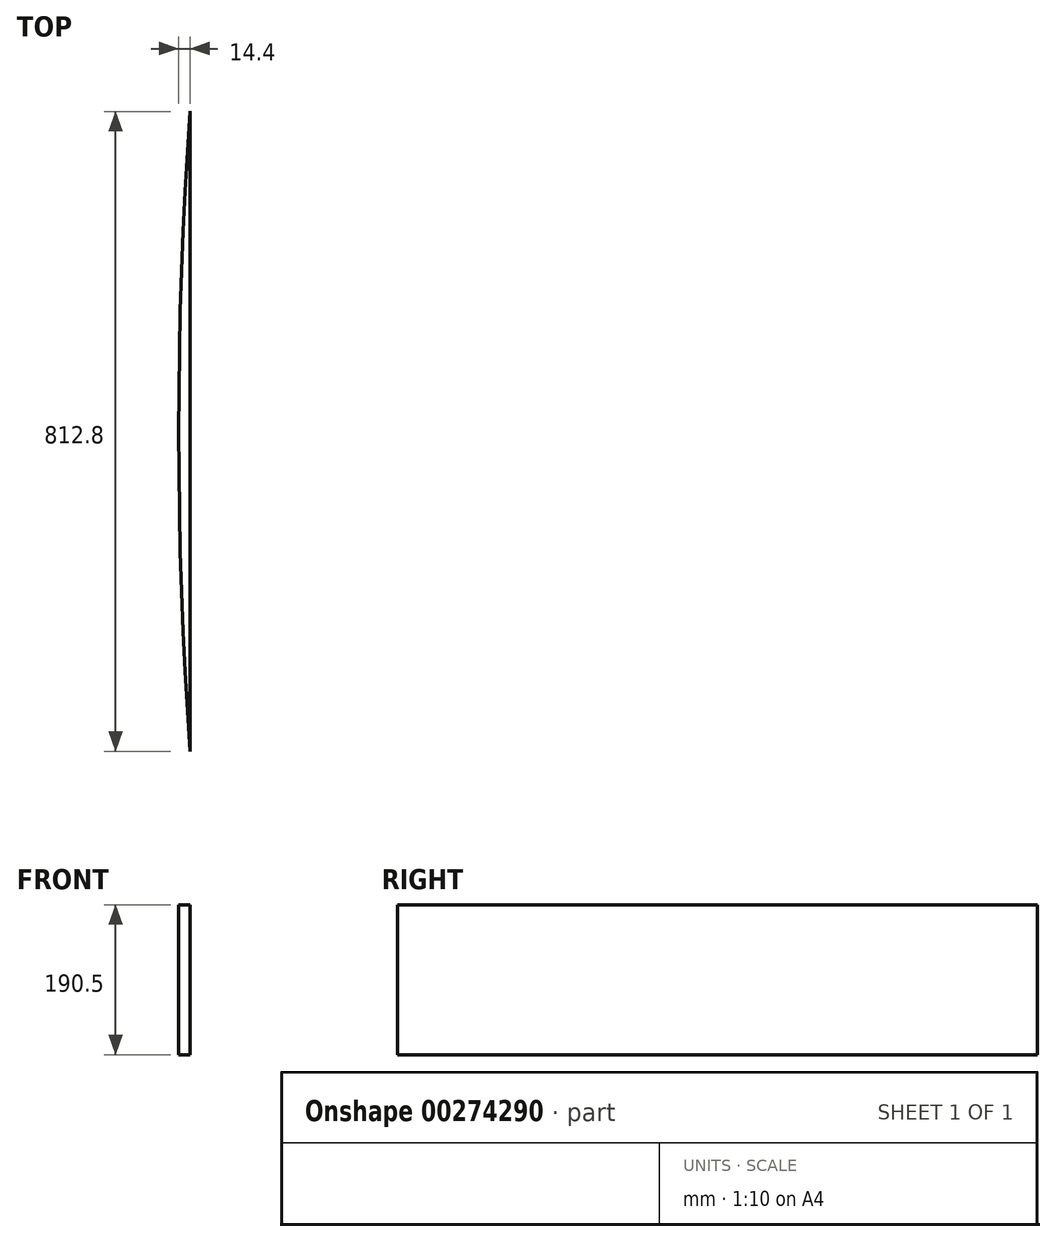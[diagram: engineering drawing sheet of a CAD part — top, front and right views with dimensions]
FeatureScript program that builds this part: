
annotation { "Feature Type Name" : "Feature", "Feature Type Description" : "" }
export const myFeature = defineFeature(function(context is Context, id is Id, definition is map)
    precondition{}
    {
        {
            var Q0;
            Q0=qCreatedBy(makeId("Top.planeOp"),FACE);
            var sketch = newSketch(context, id + "F0", { "sketchPlane" : qUnion([Q0])});
            skLineSegment(sketch, "E0", {"start": v(0, 0) * mm, "end": v(0, 406.4) * mm});
            skLineSegment(sketch, "E1", {"start": v(0, 0) * mm, "end": v(0, -406.4) * mm});
            skArc(sketch, "E2", {"start": v(0, 406.4) * mm, "mid": v(-14.4, 0) * mm, "end": v(0, -406.4) * mm});
            skSolve(sketch);
        }
        {
            var Q0;
            Q0=makeQuery(id+"F0.imprint","IMPRINT",FACE,{"disambiguationData":[TD([[makeQuery(id+"F0.imprint","IMPRINT",EDGE,{"derivedFrom":sQuery(id+"F0.wireOp",EDGE,"E0")}),1.0]])]});
            extrude(context, id + "F1", {"entities" : qUnion([Q0]), "depth" : 190.5 * mm});
        }
    });
